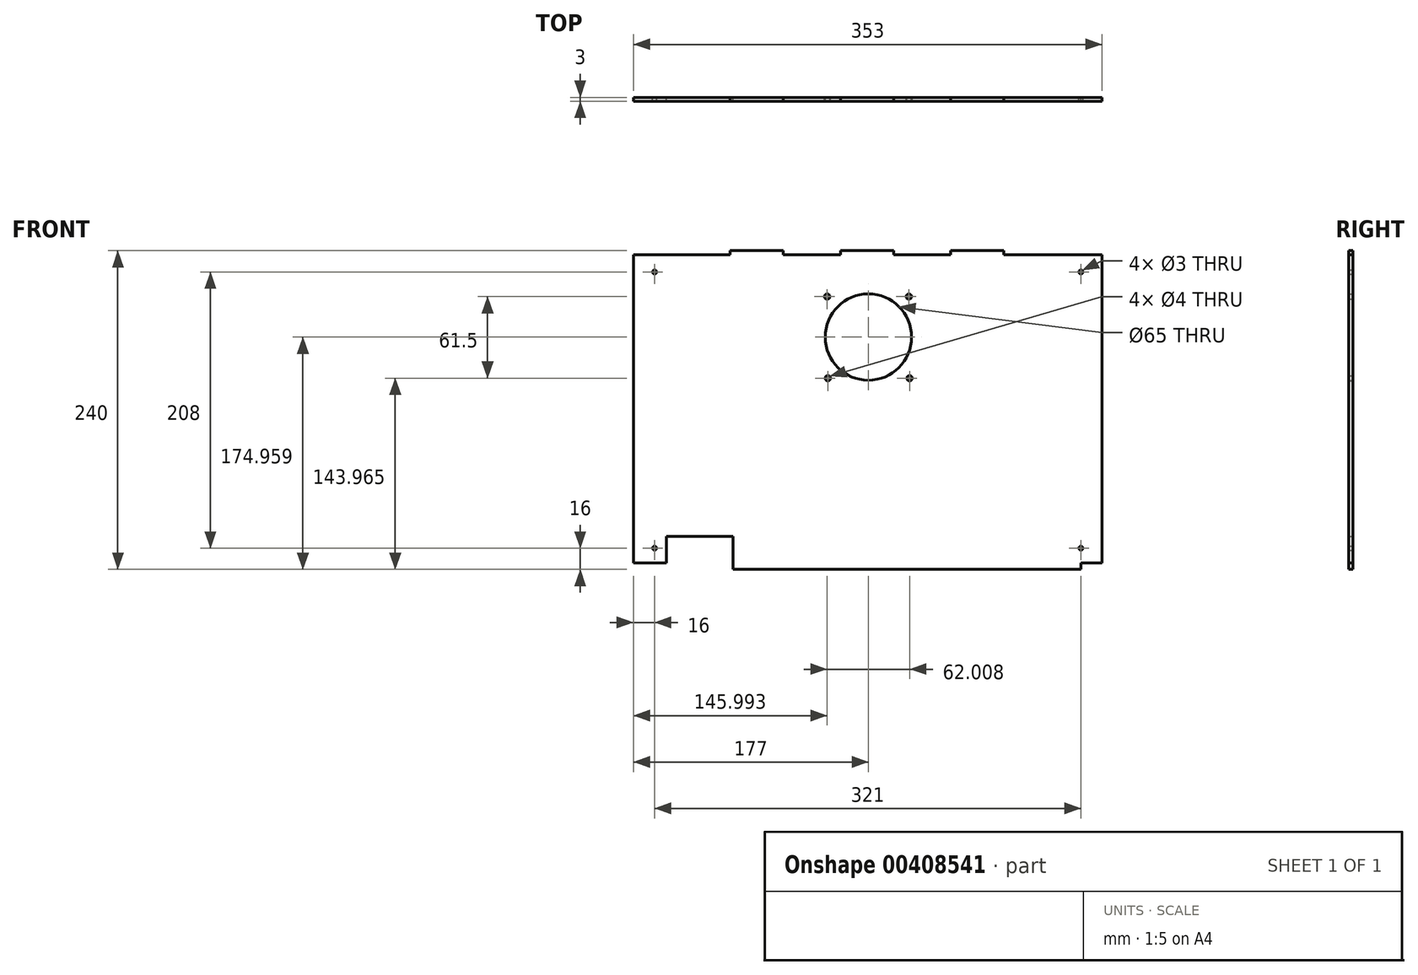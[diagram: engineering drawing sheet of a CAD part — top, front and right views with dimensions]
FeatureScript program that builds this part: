
annotation { "Feature Type Name" : "Feature", "Feature Type Description" : "" }
export const myFeature = defineFeature(function(context is Context, id is Id, definition is map)
    precondition{}
    {
        {
            var Q0;
            Q0=qCreatedBy(makeId("Front.planeOp"),FACE);
            var sketch = newSketch(context, id + "F0", { "sketchPlane" : qUnion([Q0])});
            skLineSegment(sketch, "E0.bottom", {"start": v(102, 120) * mm, "end": v(62, 120) * mm});
            skLineSegment(sketch, "E0.top", {"start": v(160, -120) * mm, "end": v(-102, -120) * mm});
            skLineSegment(sketch, "E0.left", {"start": v(176, 117) * mm, "end": v(176, -115) * mm});
            skLineSegment(sketch, "E0.right", {"start": v(-177, 117) * mm, "end": v(-177, -115) * mm});
            skPoint(sketch, "E0.middle", {"position": v(0, 0) * mm});
            skLineSegment(sketch, "E1", {"start": v(-177, -115) * mm, "end": v(-152, -115) * mm});
            skLineSegment(sketch, "E2", {"start": v(-152, -115) * mm, "end": v(-152, -95) * mm});
            skLineSegment(sketch, "E3", {"start": v(-152, -95) * mm, "end": v(-102, -95) * mm});
            skLineSegment(sketch, "E4", {"start": v(-102, -95) * mm, "end": v(-102, -120) * mm});
            skLineSegment(sketch, "E5", {"start": v(176, -115) * mm, "end": v(160, -115) * mm});
            skLineSegment(sketch, "E6", {"start": v(160, -115) * mm, "end": v(160, -120) * mm});
            skLineSegment(sketch, "E7", {"start": v(-177, 117) * mm, "end": v(-104, 117) * mm});
            skLineSegment(sketch, "E8", {"start": v(-104, 117) * mm, "end": v(-104, 120) * mm});
            skLineSegment(sketch, "E9", {"start": v(-104, 120) * mm, "end": v(-64, 120) * mm});
            skLineSegment(sketch, "E10", {"start": v(-64, 120) * mm, "end": v(-64, 117) * mm});
            skLineSegment(sketch, "E11", {"start": v(-64, 117) * mm, "end": v(-21, 117) * mm});
            skLineSegment(sketch, "E12", {"start": v(-21, 117) * mm, "end": v(-21, 120) * mm});
            skLineSegment(sketch, "E13", {"start": v(-21, 120) * mm, "end": v(19, 120) * mm});
            skLineSegment(sketch, "E14", {"start": v(19, 120) * mm, "end": v(19, 117) * mm});
            skLineSegment(sketch, "E15", {"start": v(19, 117) * mm, "end": v(62, 117) * mm});
            skLineSegment(sketch, "E16", {"start": v(62, 117) * mm, "end": v(62, 120) * mm});
            skLineSegment(sketch, "E17", {"start": v(62, 120) * mm, "end": v(102, 120) * mm});
            skLineSegment(sketch, "E18", {"start": v(102, 120) * mm, "end": v(102, 117) * mm});
            skLineSegment(sketch, "E19", {"start": v(102, 117) * mm, "end": v(176, 117) * mm});
            skLineSegment(sketch, "E20.trimOffspring", {"start": v(19, 120) * mm, "end": v(-21, 120) * mm});
            skLineSegment(sketch, "E21.trimOffspring", {"start": v(-64, 120) * mm, "end": v(-104, 120) * mm});
            skCircle(sketch, "E22", {"center": v(-161, -104) * mm, "radius": 1.5 * mm});
            skCircle(sketch, "E23", {"center": v(160, -104) * mm, "radius": 1.5 * mm});
            skCircle(sketch, "E24", {"center": v(-161, 104) * mm, "radius": 1.5 * mm});
            skCircle(sketch, "E25", {"center": v(160, 104) * mm, "radius": 1.5 * mm});
            skSolve(sketch);
        }
        {
            var Q0;
            Q0=makeQuery(id+"F0.imprint","IMPRINT",FACE,{"disambiguationData":[TD([[makeQuery(id+"F0.imprint","IMPRINT",EDGE,{"derivedFrom":sQuery(id+"F0.wireOp",EDGE,"E0.top")}),-1.0]])]});
            extrude(context, id + "F1", {"entities" : qUnion([Q0]), "depth" : 3 * mm});
        }
        {
            var Q0;
            Q0=makeQuery(id+"F1.opExtrude","CAP_FACE",FACE,{"disambiguationData":[OSD([sQuery(id+"F0.wireOp",EDGE,"E0.top"),sQuery(id+"F0.wireOp",EDGE,"E0.left"),sQuery(id+"F0.wireOp",EDGE,"E0.right"),sQuery(id+"F0.wireOp",EDGE,"E1"),sQuery(id+"F0.wireOp",EDGE,"E2"),sQuery(id+"F0.wireOp",EDGE,"E3"),sQuery(id+"F0.wireOp",EDGE,"E4"),sQuery(id+"F0.wireOp",EDGE,"E5"),sQuery(id+"F0.wireOp",EDGE,"E6"),sQuery(id+"F0.wireOp",EDGE,"E7"),sQuery(id+"F0.wireOp",EDGE,"E8"),sQuery(id+"F0.wireOp",EDGE,"E10"),sQuery(id+"F0.wireOp",EDGE,"E11"),sQuery(id+"F0.wireOp",EDGE,"E12"),sQuery(id+"F0.wireOp",EDGE,"E14"),sQuery(id+"F0.wireOp",EDGE,"E15"),sQuery(id+"F0.wireOp",EDGE,"E16"),sQuery(id+"F0.wireOp",EDGE,"E17"),sQuery(id+"F0.wireOp",EDGE,"E18"),sQuery(id+"F0.wireOp",EDGE,"E19"),sQuery(id+"F0.wireOp",EDGE,"E20.trimOffspring"),sQuery(id+"F0.wireOp",EDGE,"E21.trimOffspring")])],"isStart":true});
            var sketch = newSketch(context, id + "F2", { "sketchPlane" : qUnion([Q0])});
            skCircle(sketch, "E26", {"center": v(0, 54.96) * mm, "radius": 32.5 * mm});
            skSolve(sketch);
        }
        {
            var Q0;
            Q0=makeQuery(id+"F2.imprint","IMPRINT",FACE,{"disambiguationData":[TD([[makeQuery(id+"F2.imprint","IMPRINT",EDGE,{"derivedFrom":sQuery(id+"F2.wireOp",EDGE,"E26")}),1.0]])]});
            extrude(context, id + "F3", {"entities" : qUnion([Q0]), "operationType" : NewBodyOperationType.REMOVE, "oppositeDirection" : true, "depth" : 3 * mm});
        }
        {
            var Q0;
            Q0=makeQuery(id+"F1.opExtrude","CAP_FACE",FACE,{"disambiguationData":[OSD([sQuery(id+"F0.wireOp",EDGE,"E0.top"),sQuery(id+"F0.wireOp",EDGE,"E0.left"),sQuery(id+"F0.wireOp",EDGE,"E0.right"),sQuery(id+"F0.wireOp",EDGE,"E1"),sQuery(id+"F0.wireOp",EDGE,"E2"),sQuery(id+"F0.wireOp",EDGE,"E3"),sQuery(id+"F0.wireOp",EDGE,"E4"),sQuery(id+"F0.wireOp",EDGE,"E5"),sQuery(id+"F0.wireOp",EDGE,"E6"),sQuery(id+"F0.wireOp",EDGE,"E7"),sQuery(id+"F0.wireOp",EDGE,"E8"),sQuery(id+"F0.wireOp",EDGE,"E10"),sQuery(id+"F0.wireOp",EDGE,"E11"),sQuery(id+"F0.wireOp",EDGE,"E12"),sQuery(id+"F0.wireOp",EDGE,"E14"),sQuery(id+"F0.wireOp",EDGE,"E15"),sQuery(id+"F0.wireOp",EDGE,"E16"),sQuery(id+"F0.wireOp",EDGE,"E17"),sQuery(id+"F0.wireOp",EDGE,"E18"),sQuery(id+"F0.wireOp",EDGE,"E19"),sQuery(id+"F0.wireOp",EDGE,"E20.trimOffspring"),sQuery(id+"F0.wireOp",EDGE,"E21.trimOffspring")])],"isStart":true});
            var sketch = newSketch(context, id + "F4", { "sketchPlane" : qUnion([Q0])});
            skLineSegment(sketch, "E27.bottom", {"start": v(-30.75, 85.7) * mm, "end": v(30.75, 85.7) * mm});
            skLineSegment(sketch, "E27.top", {"start": v(-30.75, 24.2) * mm, "end": v(30.75, 24.2) * mm});
            skLineSegment(sketch, "E27.left", {"start": v(-30.75, 85.7) * mm, "end": v(-30.75, 24.2) * mm});
            skLineSegment(sketch, "E27.right", {"start": v(30.75, 85.7) * mm, "end": v(30.75, 24.2) * mm});
            skPoint(sketch, "E27.middle", {"position": v(0, 54.96) * mm});
            skSolve(sketch);
        }
        {
            var Q0;
            {var subQ0=sQuery(id+"F4.wireOp",EDGE,"E27.left");var subQ1=sQuery(id+"F4.wireOp",EDGE,"E27.bottom");var subQ2=makeQuery(id+"F4.imprint","INTERSECT",VERTEX,{"derivedFrom":[subQ1,subQ0]});Q0=makeQuery(id+"F4.imprint","IMPRINT",FACE,{"disambiguationData":[TD([[makeQuery(id+"F4.imprint","IMPRINT",EDGE,{"disambiguationData":[TD([[subQ2,-1.0]])],"derivedFrom":subQ1}),-1.0]])]});}
            var sketch = newSketch(context, id + "F5", { "sketchPlane" : qUnion([Q0])});
            skCircle(sketch, "E28", {"center": v(-30.5, 85.47) * mm, "radius": 2 * mm});
            skCircle(sketch, "E29", {"center": v(31, 85.46) * mm, "radius": 2 * mm});
            skCircle(sketch, "E30", {"center": v(30.5, 23.96) * mm, "radius": 2 * mm});
            skCircle(sketch, "E31", {"center": v(-31, 23.97) * mm, "radius": 2 * mm});
            skSolve(sketch);
        }
        {
            var Q0;
            Q0 = qSketchRegion(id + "F5", true);
            extrude(context, id + "F6", {"entities" : qUnion([Q0]), "operationType" : NewBodyOperationType.REMOVE, "oppositeDirection" : true, "depth" : 3 * mm});
        }
    });
